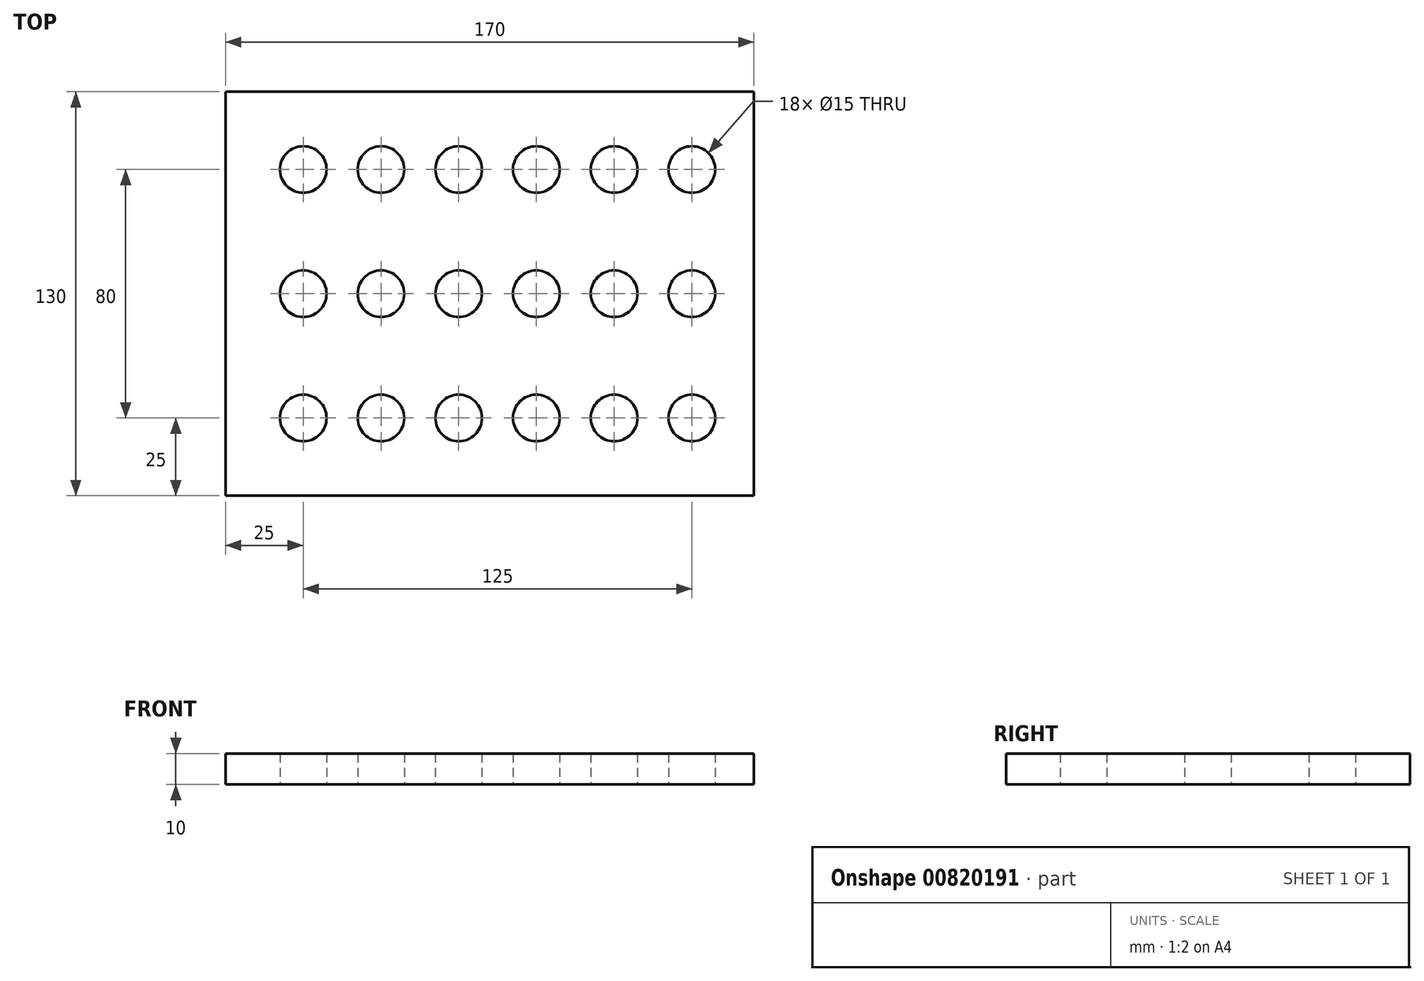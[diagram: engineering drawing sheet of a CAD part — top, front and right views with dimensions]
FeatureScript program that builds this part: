
annotation { "Feature Type Name" : "Feature", "Feature Type Description" : "" }
export const myFeature = defineFeature(function(context is Context, id is Id, definition is map)
    precondition{}
    {
        {
            var Q0;
            Q0=qCreatedBy(makeId("Top.planeOp"),FACE);
            var sketch = newSketch(context, id + "F0", { "sketchPlane" : qUnion([Q0])});
            skLineSegment(sketch, "E0.bottom", {"start": v(-85, 65) * mm, "end": v(85, 65) * mm});
            skLineSegment(sketch, "E0.top", {"start": v(-85, -65) * mm, "end": v(85, -65) * mm});
            skLineSegment(sketch, "E0.left", {"start": v(-85, 65) * mm, "end": v(-85, -65) * mm});
            skLineSegment(sketch, "E0.right", {"start": v(85, 65) * mm, "end": v(85, -65) * mm});
            skPoint(sketch, "E0.middle", {"position": v(0, 0) * mm});
            skCircle(sketch, "E1", {"center": v(-60, 40) * mm, "radius": 7.5 * mm});
            skCircle(sketch, "E2.0.1.0", {"center": v(-60, 0) * mm, "radius": 7.5 * mm});
            skCircle(sketch, "E2.0.2.0", {"center": v(-60, -40) * mm, "radius": 7.5 * mm});
            skCircle(sketch, "E2.1.0.0", {"center": v(-35, 40) * mm, "radius": 7.5 * mm});
            skCircle(sketch, "E2.1.1.0", {"center": v(-35, 0) * mm, "radius": 7.5 * mm});
            skCircle(sketch, "E2.1.2.0", {"center": v(-35, -40) * mm, "radius": 7.5 * mm});
            skCircle(sketch, "E2.2.0.0", {"center": v(-10, 40) * mm, "radius": 7.5 * mm});
            skCircle(sketch, "E2.2.1.0", {"center": v(-10, 0) * mm, "radius": 7.5 * mm});
            skCircle(sketch, "E2.2.2.0", {"center": v(-10, -40) * mm, "radius": 7.5 * mm});
            skCircle(sketch, "E2.3.0.0", {"center": v(15, 40) * mm, "radius": 7.5 * mm});
            skCircle(sketch, "E2.3.1.0", {"center": v(15, 0) * mm, "radius": 7.5 * mm});
            skCircle(sketch, "E2.3.2.0", {"center": v(15, -40) * mm, "radius": 7.5 * mm});
            skCircle(sketch, "E2.4.0.0", {"center": v(40, 40) * mm, "radius": 7.5 * mm});
            skCircle(sketch, "E2.4.1.0", {"center": v(40, 0) * mm, "radius": 7.5 * mm});
            skCircle(sketch, "E2.4.2.0", {"center": v(40, -40) * mm, "radius": 7.5 * mm});
            skCircle(sketch, "E2.5.0.0", {"center": v(65, 40) * mm, "radius": 7.5 * mm});
            skCircle(sketch, "E2.5.1.0", {"center": v(65, 0) * mm, "radius": 7.5 * mm});
            skCircle(sketch, "E2.5.2.0", {"center": v(65, -40) * mm, "radius": 7.5 * mm});
            skLineSegment(sketch, "E2.direction1", {"start": v(-60, 40) * mm, "end": v(-35, 40) * mm, "construction": true});
            skLineSegment(sketch, "E2.direction2", {"start": v(-60, 40) * mm, "end": v(-60, 0) * mm, "construction": true});
            skSolve(sketch);
        }
        {
            var Q0;
            Q0 = qSketchRegion(id + "F0", true);
            extrude(context, id + "F1", {"entities" : qUnion([Q0]), "depth" : 10 * mm, "offsetDistance" : 25.4 * mm});
        }
    });
